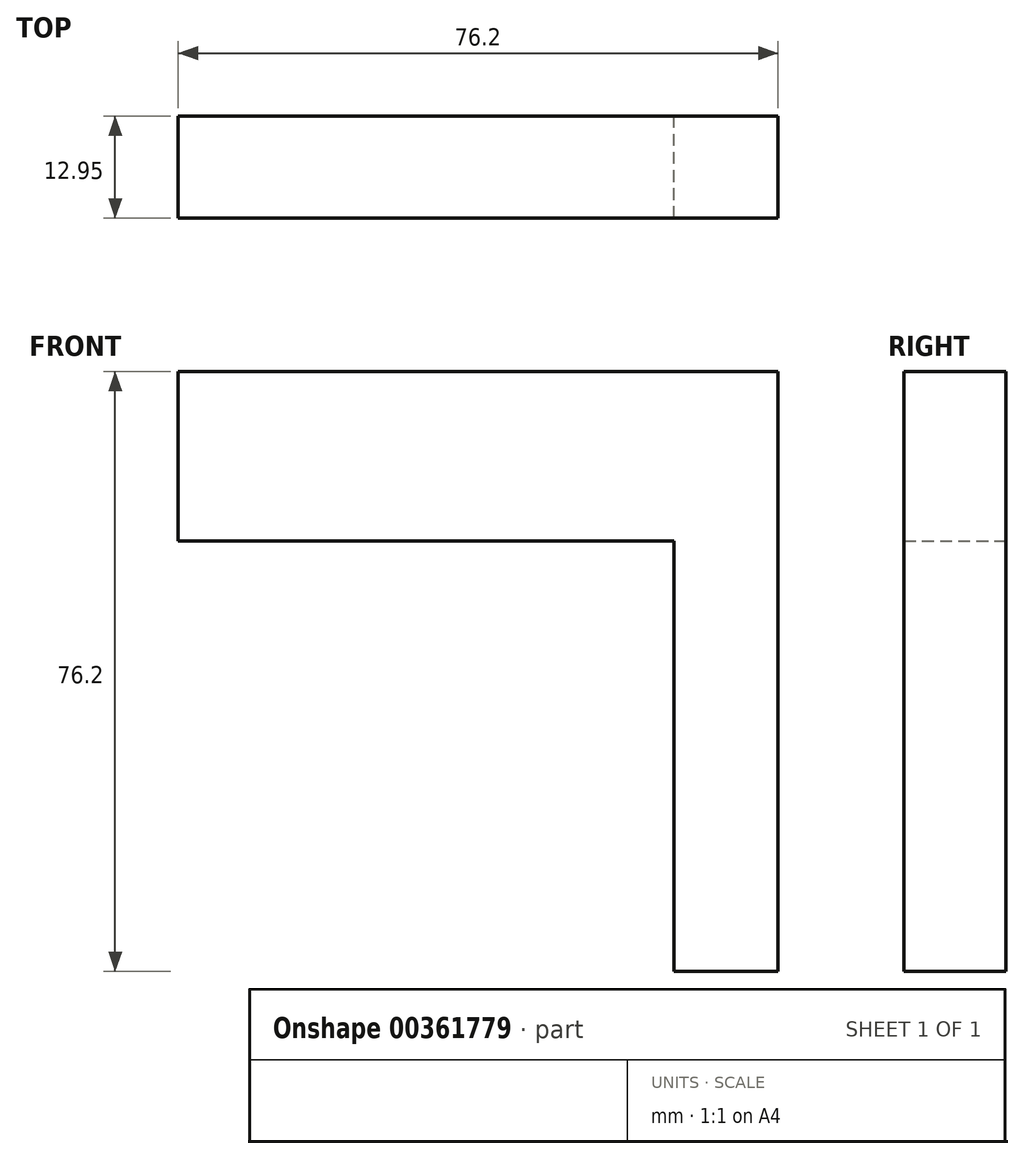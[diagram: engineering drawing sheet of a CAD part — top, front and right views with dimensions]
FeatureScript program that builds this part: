
annotation { "Feature Type Name" : "Feature", "Feature Type Description" : "" }
export const myFeature = defineFeature(function(context is Context, id is Id, definition is map)
    precondition{}
    {
        {
            var Q0;
            Q0=qCreatedBy(makeId("Front.planeOp"),FACE);
            var sketch = newSketch(context, id + "F0", { "sketchPlane" : qUnion([Q0])});
            skLineSegment(sketch, "E0", {"start": v(43.92, 38.03) * mm, "end": v(43.92, -16.66) * mm});
            skLineSegment(sketch, "E1", {"start": v(30.72, -16.66) * mm, "end": v(43.92, -16.66) * mm});
            skLineSegment(sketch, "E2", {"start": v(30.72, -16.66) * mm, "end": v(30.72, 38.03) * mm});
            skLineSegment(sketch, "E3", {"start": v(30.72, 38.03) * mm, "end": v(-32.28, 38.03) * mm});
            skLineSegment(sketch, "E4", {"start": v(-32.28, 38.03) * mm, "end": v(-32.28, 59.54) * mm});
            skLineSegment(sketch, "E5", {"start": v(-32.28, 59.54) * mm, "end": v(43.92, 59.54) * mm});
            skLineSegment(sketch, "E6", {"start": v(43.92, 59.54) * mm, "end": v(43.92, 38.03) * mm});
            skSolve(sketch);
        }
        {
            var Q0;
            Q0=makeQuery(id+"F0.imprint","IMPRINT",FACE,{"disambiguationData":[TD([[makeQuery(id+"F0.imprint","IMPRINT",EDGE,{"derivedFrom":sQuery(id+"F0.wireOp",EDGE,"E0")}),-1.0]])]});
            extrude(context, id + "F1", {"entities" : qUnion([Q0]), "depth" : 12.95 * mm});
        }
    });
